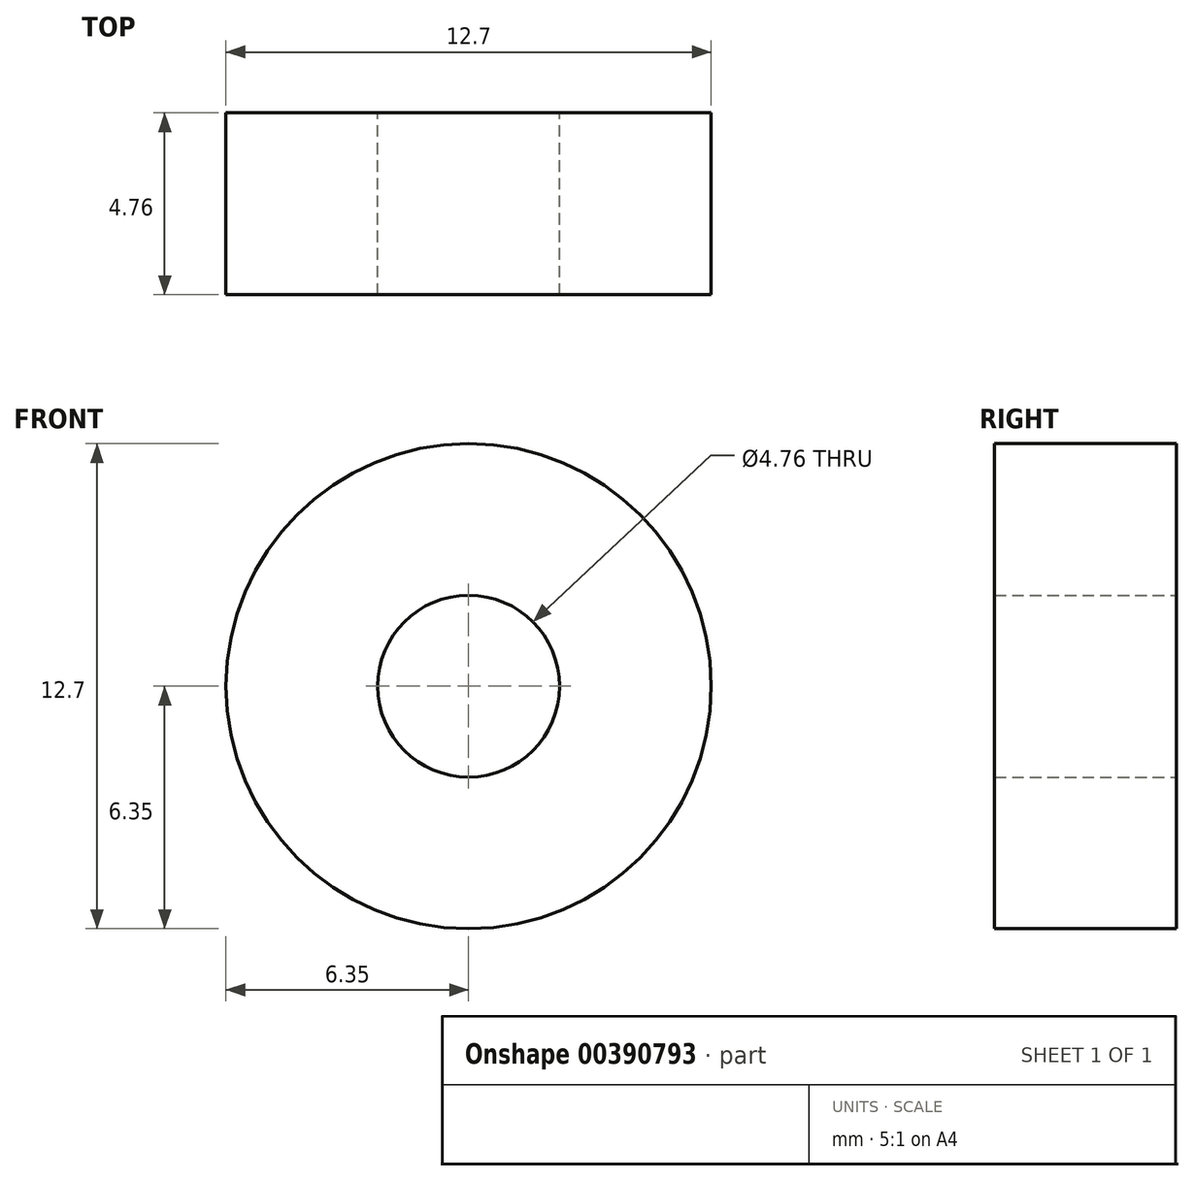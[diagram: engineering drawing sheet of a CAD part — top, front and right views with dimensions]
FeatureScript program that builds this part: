
annotation { "Feature Type Name" : "Feature", "Feature Type Description" : "" }
export const myFeature = defineFeature(function(context is Context, id is Id, definition is map)
    precondition{}
    {
        {
            var Q0;
            Q0=qCreatedBy(makeId("Front.planeOp"),FACE);
            var sketch = newSketch(context, id + "F0", { "sketchPlane" : qUnion([Q0]), "asVersion" : FeatureScriptVersionNumber.V593_MASTER_MODEL_DOC});
            skCircle(sketch, "E0", {"center": v(0, 0) * mm, "radius": 2.38 * mm});
            skCircle(sketch, "E1", {"center": v(0, 0) * mm, "radius": 6.35 * mm});
            skSolve(sketch);
        }
        {
            var Q0;
            Q0=makeQuery(id+"F0.imprint","IMPRINT",FACE,{"disambiguationData":[TD([[makeQuery(id+"F0.imprint","IMPRINT",EDGE,{"derivedFrom":sQuery(id+"F0.wireOp",EDGE,"E0")}),-1.0]])]});
            extrude(context, id + "F1", {"entities" : qUnion([Q0]), "depth" : 4.76 * mm, "offsetDistance" : 25 * mm});
        }
    });
